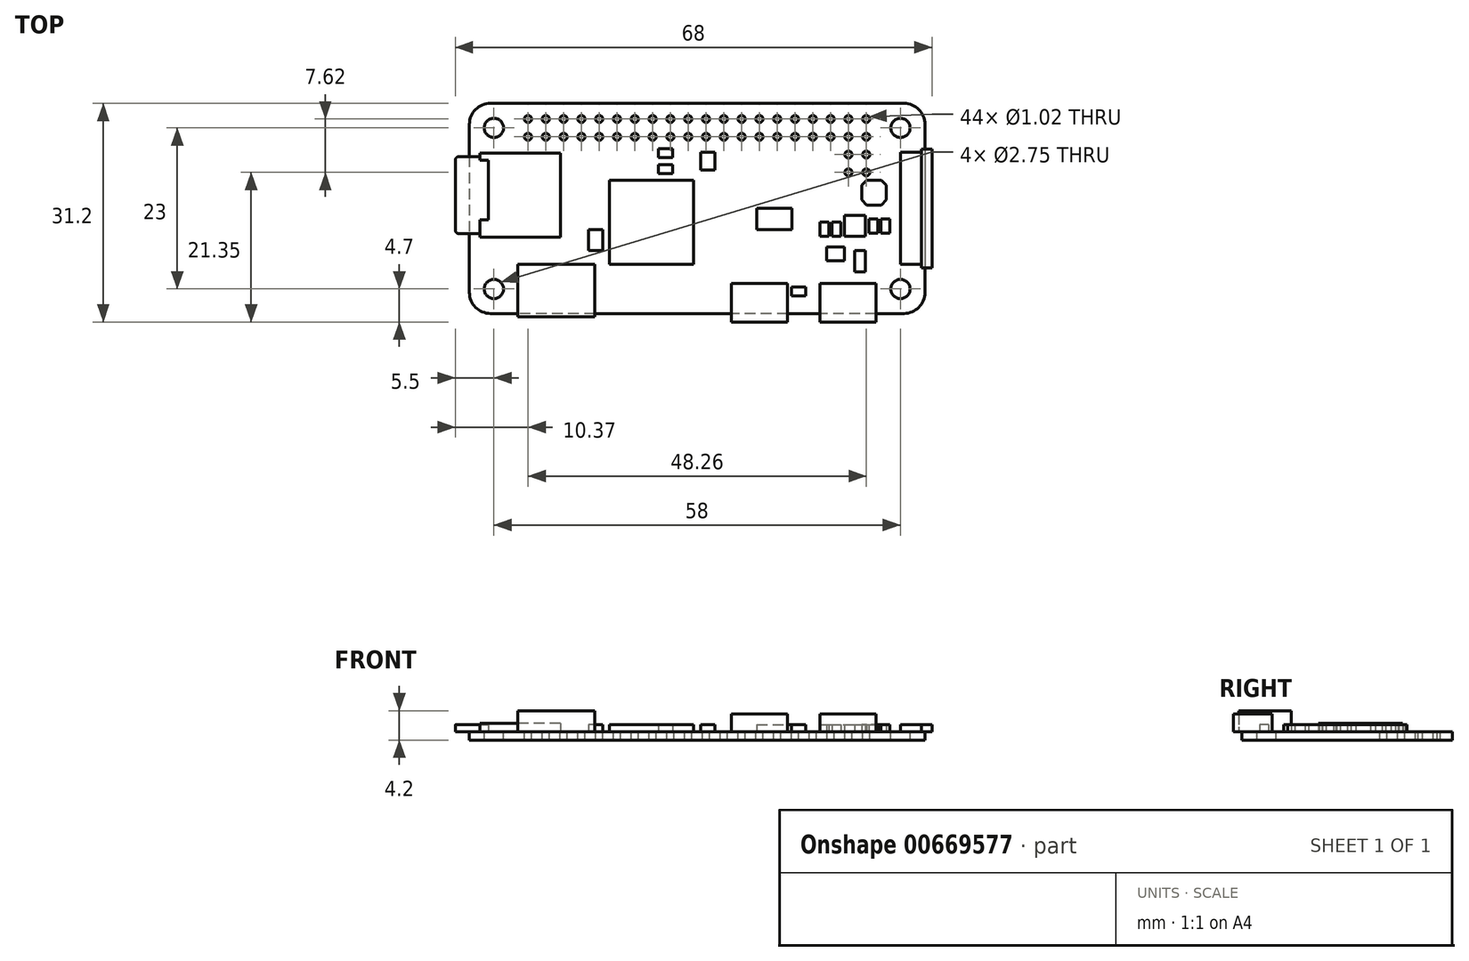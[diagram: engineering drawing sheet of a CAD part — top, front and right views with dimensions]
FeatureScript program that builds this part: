
annotation { "Feature Type Name" : "Feature", "Feature Type Description" : "" }
export const myFeature = defineFeature(function(context is Context, id is Id, definition is map)
    precondition{}
    {
        {
            var Q0;
            Q0=qCreatedBy(makeId("Top.planeOp"),FACE);
            var sketch = newSketch(context, id + "F0", { "sketchPlane" : qUnion([Q0])});
            skLineSegment(sketch, "E0.bottom", {"start": v(29.5, 15) * mm, "end": v(-29.5, 15) * mm});
            skLineSegment(sketch, "E0.top", {"start": v(29.5, -15) * mm, "end": v(-29.5, -15) * mm});
            skLineSegment(sketch, "E0.left", {"start": v(32.5, 12) * mm, "end": v(32.5, -12) * mm});
            skLineSegment(sketch, "E0.right", {"start": v(-32.5, 12) * mm, "end": v(-32.5, -12) * mm});
            skPoint(sketch, "E0.middle", {"position": v(0, 0) * mm});
            skPoint(sketch, "E1.visualSharp", {"position": v(-32.5, 15) * mm});
            skArc(sketch, "E1.filletArc", {"start": v(-29.5, 15) * mm, "mid": v(-31.62, 14.12) * mm, "end": v(-32.5, 12) * mm});
            skPoint(sketch, "E2.visualSharp", {"position": v(32.5, 15) * mm});
            skArc(sketch, "E2.filletArc", {"start": v(32.5, 12) * mm, "mid": v(31.62, 14.12) * mm, "end": v(29.5, 15) * mm});
            skPoint(sketch, "E3.visualSharp", {"position": v(32.5, -15) * mm});
            skArc(sketch, "E3.filletArc", {"start": v(29.5, -15) * mm, "mid": v(31.62, -14.12) * mm, "end": v(32.5, -12) * mm});
            skPoint(sketch, "E4.visualSharp", {"position": v(-32.5, -15) * mm});
            skArc(sketch, "E4.filletArc", {"start": v(-32.5, -12) * mm, "mid": v(-31.62, -14.12) * mm, "end": v(-29.5, -15) * mm});
            skLineSegment(sketch, "E5.bottom", {"start": v(29, 11.5) * mm, "end": v(-29, 11.5) * mm, "construction": true});
            skLineSegment(sketch, "E5.top", {"start": v(29, -11.5) * mm, "end": v(-29, -11.5) * mm, "construction": true});
            skLineSegment(sketch, "E5.left", {"start": v(29, 11.5) * mm, "end": v(29, -11.5) * mm, "construction": true});
            skLineSegment(sketch, "E5.right", {"start": v(-29, 11.5) * mm, "end": v(-29, -11.5) * mm, "construction": true});
            skCircle(sketch, "E6", {"center": v(29, 11.5) * mm, "radius": 3 * mm});
            skCircle(sketch, "E7", {"center": v(29, 11.5) * mm, "radius": 1.38 * mm});
            skCircle(sketch, "E8", {"center": v(-29, 11.5) * mm, "radius": 1.38 * mm});
            skCircle(sketch, "E9", {"center": v(-29, 11.5) * mm, "radius": 3 * mm});
            skCircle(sketch, "E10", {"center": v(-29, -11.5) * mm, "radius": 3 * mm});
            skCircle(sketch, "E11", {"center": v(-29, -11.5) * mm, "radius": 1.38 * mm});
            skCircle(sketch, "E12", {"center": v(29, -11.5) * mm, "radius": 1.38 * mm});
            skCircle(sketch, "E13", {"center": v(29, -11.5) * mm, "radius": 3 * mm});
            skCircle(sketch, "E14", {"center": v(24.13, 12.77) * mm, "radius": 0.5 * mm});
            skCircle(sketch, "E15", {"center": v(24.13, 10.23) * mm, "radius": 0.5 * mm});
            skLineSegment(sketch, "E16", {"start": v(24.13, 12.77) * mm, "end": v(24.13, 10.23) * mm, "construction": true});
            skPoint(sketch, "E17", {"position": v(24.13, 11.5) * mm});
            skCircle(sketch, "E18.1.0.0", {"center": v(21.59, 12.77) * mm, "radius": 0.5 * mm});
            skCircle(sketch, "E18.1.0.1", {"center": v(21.59, 10.23) * mm, "radius": 0.5 * mm});
            skCircle(sketch, "E18.2.0.0", {"center": v(19.05, 12.77) * mm, "radius": 0.5 * mm});
            skCircle(sketch, "E18.2.0.1", {"center": v(19.05, 10.23) * mm, "radius": 0.5 * mm});
            skCircle(sketch, "E18.3.0.0", {"center": v(16.5, 12.77) * mm, "radius": 0.5 * mm});
            skCircle(sketch, "E18.3.0.1", {"center": v(16.5, 10.23) * mm, "radius": 0.5 * mm});
            skCircle(sketch, "E18.4.0.0", {"center": v(13.97, 12.77) * mm, "radius": 0.5 * mm});
            skCircle(sketch, "E18.4.0.1", {"center": v(13.97, 10.23) * mm, "radius": 0.5 * mm});
            skCircle(sketch, "E18.5.0.0", {"center": v(11.43, 12.77) * mm, "radius": 0.5 * mm});
            skCircle(sketch, "E18.5.0.1", {"center": v(11.43, 10.23) * mm, "radius": 0.5 * mm});
            skCircle(sketch, "E18.6.0.0", {"center": v(8.89, 12.77) * mm, "radius": 0.5 * mm});
            skCircle(sketch, "E18.6.0.1", {"center": v(8.89, 10.23) * mm, "radius": 0.5 * mm});
            skCircle(sketch, "E18.7.0.0", {"center": v(6.35, 12.77) * mm, "radius": 0.5 * mm});
            skCircle(sketch, "E18.7.0.1", {"center": v(6.35, 10.23) * mm, "radius": 0.5 * mm});
            skCircle(sketch, "E18.8.0.0", {"center": v(3.8, 12.77) * mm, "radius": 0.5 * mm});
            skCircle(sketch, "E18.8.0.1", {"center": v(3.8, 10.23) * mm, "radius": 0.5 * mm});
            skCircle(sketch, "E18.9.0.0", {"center": v(1.27, 12.77) * mm, "radius": 0.5 * mm});
            skCircle(sketch, "E18.9.0.1", {"center": v(1.27, 10.23) * mm, "radius": 0.5 * mm});
            skCircle(sketch, "E18.10.0.0", {"center": v(-1.27, 12.77) * mm, "radius": 0.5 * mm});
            skCircle(sketch, "E18.10.0.1", {"center": v(-1.27, 10.23) * mm, "radius": 0.5 * mm});
            skCircle(sketch, "E18.11.0.0", {"center": v(-3.81, 12.77) * mm, "radius": 0.5 * mm});
            skCircle(sketch, "E18.11.0.1", {"center": v(-3.81, 10.23) * mm, "radius": 0.5 * mm});
            skCircle(sketch, "E18.12.0.0", {"center": v(-6.35, 12.77) * mm, "radius": 0.5 * mm});
            skCircle(sketch, "E18.12.0.1", {"center": v(-6.35, 10.23) * mm, "radius": 0.5 * mm});
            skCircle(sketch, "E18.13.0.0", {"center": v(-8.9, 12.77) * mm, "radius": 0.5 * mm});
            skCircle(sketch, "E18.13.0.1", {"center": v(-8.9, 10.23) * mm, "radius": 0.5 * mm});
            skCircle(sketch, "E18.14.0.0", {"center": v(-11.43, 12.77) * mm, "radius": 0.5 * mm});
            skCircle(sketch, "E18.14.0.1", {"center": v(-11.43, 10.23) * mm, "radius": 0.5 * mm});
            skCircle(sketch, "E18.15.0.0", {"center": v(-13.97, 12.77) * mm, "radius": 0.5 * mm});
            skCircle(sketch, "E18.15.0.1", {"center": v(-13.97, 10.23) * mm, "radius": 0.5 * mm});
            skCircle(sketch, "E18.16.0.0", {"center": v(-16.51, 12.77) * mm, "radius": 0.5 * mm});
            skCircle(sketch, "E18.16.0.1", {"center": v(-16.51, 10.23) * mm, "radius": 0.5 * mm});
            skCircle(sketch, "E18.17.0.0", {"center": v(-19.05, 12.77) * mm, "radius": 0.5 * mm});
            skCircle(sketch, "E18.17.0.1", {"center": v(-19.05, 10.23) * mm, "radius": 0.5 * mm});
            skCircle(sketch, "E18.18.0.0", {"center": v(-21.6, 12.77) * mm, "radius": 0.5 * mm});
            skCircle(sketch, "E18.18.0.1", {"center": v(-21.6, 10.23) * mm, "radius": 0.5 * mm});
            skCircle(sketch, "E18.19.0.0", {"center": v(-24.13, 12.77) * mm, "radius": 0.5 * mm});
            skCircle(sketch, "E18.19.0.1", {"center": v(-24.13, 10.23) * mm, "radius": 0.5 * mm});
            skLineSegment(sketch, "E18.direction1", {"start": v(24.13, 12.77) * mm, "end": v(21.59, 12.77) * mm, "construction": true});
            skCircle(sketch, "E19.1.0.0", {"center": v(21.59, 7.69) * mm, "radius": 0.5 * mm});
            skCircle(sketch, "E19.1.0.1", {"center": v(24.13, 7.69) * mm, "radius": 0.5 * mm});
            skCircle(sketch, "E19.1.0.2", {"center": v(24.13, 5.15) * mm, "radius": 0.5 * mm});
            skCircle(sketch, "E19.1.0.3", {"center": v(21.59, 5.15) * mm, "radius": 0.5 * mm});
            skLineSegment(sketch, "E19.direction1", {"start": v(21.59, 12.77) * mm, "end": v(21.59, 7.69) * mm, "construction": true});
            skSolve(sketch);
        }
        {
            var Q0;
            Q0=qCreatedBy(makeId("Top.planeOp"),FACE);
            var sketch = newSketch(context, id + "F1", { "sketchPlane" : qUnion([Q0])});
            skLineSegment(sketch, "E20.bottom", {"start": v(33.5, -8.5) * mm, "end": v(32, -8.5) * mm});
            skLineSegment(sketch, "E20.top", {"start": v(33.5, 8.5) * mm, "end": v(32, 8.5) * mm});
            skLineSegment(sketch, "E20.left", {"start": v(33.5, -8.5) * mm, "end": v(33.5, 8.5) * mm});
            skLineSegment(sketch, "E20.right", {"start": v(32, -8.5) * mm, "end": v(32, 8.5) * mm});
            skPoint(sketch, "E20.middle", {"position": v(32.75, 0) * mm});
            skLineSegment(sketch, "E21.bottom", {"start": v(-14.6, -15.5) * mm, "end": v(-25.6, -15.5) * mm});
            skLineSegment(sketch, "E21.top", {"start": v(-14.6, -8) * mm, "end": v(-25.6, -8) * mm});
            skLineSegment(sketch, "E21.left", {"start": v(-14.6, -15.5) * mm, "end": v(-14.6, -8) * mm});
            skLineSegment(sketch, "E21.right", {"start": v(-25.6, -15.5) * mm, "end": v(-25.6, -8) * mm});
            skPoint(sketch, "E21.middle", {"position": v(-20.1, -11.75) * mm});
            skLineSegment(sketch, "E22.bottom", {"start": v(12.9, -16.2) * mm, "end": v(4.9, -16.2) * mm});
            skLineSegment(sketch, "E22.top", {"start": v(12.9, -10.7) * mm, "end": v(4.9, -10.7) * mm});
            skLineSegment(sketch, "E22.left", {"start": v(12.9, -16.2) * mm, "end": v(12.9, -10.7) * mm});
            skLineSegment(sketch, "E22.right", {"start": v(4.9, -16.2) * mm, "end": v(4.9, -10.7) * mm});
            skPoint(sketch, "E22.middle", {"position": v(8.9, -13.45) * mm});
            skLineSegment(sketch, "E23.bottom", {"start": v(25.5, -16.2) * mm, "end": v(17.5, -16.2) * mm});
            skLineSegment(sketch, "E23.top", {"start": v(25.5, -10.7) * mm, "end": v(17.5, -10.7) * mm});
            skLineSegment(sketch, "E23.left", {"start": v(25.5, -16.2) * mm, "end": v(25.5, -10.7) * mm});
            skLineSegment(sketch, "E23.right", {"start": v(17.5, -16.2) * mm, "end": v(17.5, -10.7) * mm});
            skPoint(sketch, "E23.middle", {"position": v(21.5, -13.45) * mm});
            skLineSegment(sketch, "E24.bottom", {"start": v(-19.5, 7.9) * mm, "end": v(-31, 7.9) * mm});
            skLineSegment(sketch, "E24.top", {"start": v(-19.5, -4.1) * mm, "end": v(-31, -4.1) * mm});
            skLineSegment(sketch, "E24.left", {"start": v(-19.5, 7.9) * mm, "end": v(-19.5, -4.1) * mm});
            skLineSegment(sketch, "E24.right", {"start": v(-31, 7.9) * mm, "end": v(-31, -4.1) * mm});
            skPoint(sketch, "E24.middle", {"position": v(-25.25, 1.9) * mm});
            skLineSegment(sketch, "E25", {"start": v(-31, 7.4) * mm, "end": v(-34, 7.4) * mm});
            skLineSegment(sketch, "E26", {"start": v(-34.5, 6.9) * mm, "end": v(-34.5, -3.1) * mm});
            skLineSegment(sketch, "E27", {"start": v(-34, -3.6) * mm, "end": v(-31, -3.6) * mm});
            skPoint(sketch, "E28.visualSharp", {"position": v(-34.5, 7.4) * mm});
            skArc(sketch, "E28.filletArc", {"start": v(-34, 7.4) * mm, "mid": v(-34.35, 7.25) * mm, "end": v(-34.5, 6.9) * mm});
            skPoint(sketch, "E29.visualSharp", {"position": v(-34.5, -3.6) * mm});
            skArc(sketch, "E29.filletArc", {"start": v(-34.5, -3.1) * mm, "mid": v(-34.35, -3.45) * mm, "end": v(-34, -3.6) * mm});
            skPoint(sketch, "E30", {"position": v(-34.5, 1.9) * mm});
            skLineSegment(sketch, "E31", {"start": v(-31, 6.9) * mm, "end": v(-29.8, 6.9) * mm});
            skLineSegment(sketch, "E32", {"start": v(-29.8, 6.9) * mm, "end": v(-29.8, -1.6) * mm});
            skLineSegment(sketch, "E33", {"start": v(-29.8, -1.6) * mm, "end": v(-31, -1.6) * mm});
            skLineSegment(sketch, "E34", {"start": v(32, 8) * mm, "end": v(29, 8) * mm});
            skLineSegment(sketch, "E35", {"start": v(29, 8) * mm, "end": v(29, -8) * mm});
            skLineSegment(sketch, "E36", {"start": v(29, -8) * mm, "end": v(32, -8) * mm});
            skLineSegment(sketch, "E37", {"start": v(32.75, 0) * mm, "end": v(29, 0) * mm, "construction": true});
            skSolve(sketch);
        }
        {
            var Q0;
            Q0=qCreatedBy(makeId("Top.planeOp"),FACE);
            var sketch = newSketch(context, id + "F2", { "sketchPlane" : qUnion([Q0])});
            skLineSegment(sketch, "E38.bottom", {"start": v(-12.5, -8) * mm, "end": v(-0.5, -8) * mm});
            skLineSegment(sketch, "E38.top", {"start": v(-12.5, 4) * mm, "end": v(-0.5, 4) * mm});
            skLineSegment(sketch, "E38.left", {"start": v(-12.5, -8) * mm, "end": v(-12.5, 4) * mm});
            skLineSegment(sketch, "E38.right", {"start": v(-0.5, -8) * mm, "end": v(-0.5, 4) * mm});
            skLineSegment(sketch, "E39.bottom", {"start": v(-5.53, 8.54) * mm, "end": v(-3.5, 8.54) * mm});
            skLineSegment(sketch, "E39.top", {"start": v(-5.53, 7.27) * mm, "end": v(-3.5, 7.27) * mm});
            skLineSegment(sketch, "E39.left", {"start": v(-5.53, 8.54) * mm, "end": v(-5.53, 7.27) * mm});
            skLineSegment(sketch, "E39.right", {"start": v(-3.5, 8.54) * mm, "end": v(-3.5, 7.27) * mm});
            skLineSegment(sketch, "E40.bottom", {"start": v(-5.53, 6.27) * mm, "end": v(-3.5, 6.27) * mm});
            skLineSegment(sketch, "E40.top", {"start": v(-5.53, 5) * mm, "end": v(-3.5, 5) * mm});
            skLineSegment(sketch, "E40.left", {"start": v(-5.53, 6.27) * mm, "end": v(-5.53, 5) * mm});
            skLineSegment(sketch, "E40.right", {"start": v(-3.5, 6.27) * mm, "end": v(-3.5, 5) * mm});
            skLineSegment(sketch, "E41.bottom", {"start": v(13.47, -11.23) * mm, "end": v(15.5, -11.23) * mm});
            skLineSegment(sketch, "E41.top", {"start": v(13.47, -12.5) * mm, "end": v(15.5, -12.5) * mm});
            skLineSegment(sketch, "E41.left", {"start": v(13.47, -11.23) * mm, "end": v(13.47, -12.5) * mm});
            skLineSegment(sketch, "E41.right", {"start": v(15.5, -11.23) * mm, "end": v(15.5, -12.5) * mm});
            skLineSegment(sketch, "E42.bottom", {"start": v(17.5, -1.97) * mm, "end": v(18.77, -1.97) * mm});
            skLineSegment(sketch, "E42.top", {"start": v(17.5, -4) * mm, "end": v(18.77, -4) * mm});
            skLineSegment(sketch, "E42.left", {"start": v(17.5, -1.97) * mm, "end": v(17.5, -4) * mm});
            skLineSegment(sketch, "E42.right", {"start": v(18.77, -1.97) * mm, "end": v(18.77, -4) * mm});
            skLineSegment(sketch, "E43.bottom", {"start": v(19.25, -1.97) * mm, "end": v(20.52, -1.97) * mm});
            skLineSegment(sketch, "E43.top", {"start": v(19.25, -4) * mm, "end": v(20.52, -4) * mm});
            skLineSegment(sketch, "E43.left", {"start": v(19.25, -1.97) * mm, "end": v(19.25, -4) * mm});
            skLineSegment(sketch, "E43.right", {"start": v(20.52, -1.97) * mm, "end": v(20.52, -4) * mm});
            skLineSegment(sketch, "E44.bottom", {"start": v(24.48, -1.48) * mm, "end": v(25.75, -1.48) * mm});
            skLineSegment(sketch, "E44.top", {"start": v(24.48, -3.52) * mm, "end": v(25.75, -3.52) * mm});
            skLineSegment(sketch, "E44.left", {"start": v(24.48, -1.48) * mm, "end": v(24.48, -3.52) * mm});
            skLineSegment(sketch, "E44.right", {"start": v(25.75, -1.48) * mm, "end": v(25.75, -3.52) * mm});
            skLineSegment(sketch, "E45.bottom", {"start": v(26.23, -1.48) * mm, "end": v(27.5, -1.48) * mm});
            skLineSegment(sketch, "E45.top", {"start": v(26.23, -3.52) * mm, "end": v(27.5, -3.52) * mm});
            skLineSegment(sketch, "E45.left", {"start": v(26.23, -1.48) * mm, "end": v(26.23, -3.52) * mm});
            skLineSegment(sketch, "E45.right", {"start": v(27.5, -1.48) * mm, "end": v(27.5, -3.52) * mm});
            skLineSegment(sketch, "E46.bottom", {"start": v(-13.5, -3) * mm, "end": v(-15.5, -3) * mm});
            skLineSegment(sketch, "E46.top", {"start": v(-13.5, -6) * mm, "end": v(-15.5, -6) * mm});
            skLineSegment(sketch, "E46.left", {"start": v(-13.5, -3) * mm, "end": v(-13.5, -6) * mm});
            skLineSegment(sketch, "E46.right", {"start": v(-15.5, -3) * mm, "end": v(-15.5, -6) * mm});
            skLineSegment(sketch, "E47.bottom", {"start": v(8.5, 0) * mm, "end": v(13.5, 0) * mm});
            skLineSegment(sketch, "E47.top", {"start": v(8.5, -3) * mm, "end": v(13.5, -3) * mm});
            skLineSegment(sketch, "E47.left", {"start": v(8.5, 0) * mm, "end": v(8.5, -3) * mm});
            skLineSegment(sketch, "E47.right", {"start": v(13.5, 0) * mm, "end": v(13.5, -3) * mm});
            skLineSegment(sketch, "E48.bottom", {"start": v(21, -1) * mm, "end": v(24, -1) * mm});
            skLineSegment(sketch, "E48.top", {"start": v(21, -4) * mm, "end": v(24, -4) * mm});
            skLineSegment(sketch, "E48.left", {"start": v(21, -1) * mm, "end": v(21, -4) * mm});
            skLineSegment(sketch, "E48.right", {"start": v(24, -1) * mm, "end": v(24, -4) * mm});
            skLineSegment(sketch, "E49.bottom", {"start": v(0.5, 8) * mm, "end": v(2.5, 8) * mm});
            skLineSegment(sketch, "E49.top", {"start": v(0.5, 5.5) * mm, "end": v(2.5, 5.5) * mm});
            skLineSegment(sketch, "E49.left", {"start": v(0.5, 8) * mm, "end": v(0.5, 5.5) * mm});
            skLineSegment(sketch, "E49.right", {"start": v(2.5, 8) * mm, "end": v(2.5, 5.5) * mm});
            skLineSegment(sketch, "E50.bottom", {"start": v(18.5, -5.5) * mm, "end": v(21, -5.5) * mm});
            skLineSegment(sketch, "E50.top", {"start": v(18.5, -7.5) * mm, "end": v(21, -7.5) * mm});
            skLineSegment(sketch, "E50.left", {"start": v(18.5, -5.5) * mm, "end": v(18.5, -7.5) * mm});
            skLineSegment(sketch, "E50.right", {"start": v(21, -5.5) * mm, "end": v(21, -7.5) * mm});
            skLineSegment(sketch, "E51.bottom", {"start": v(22.48, -6) * mm, "end": v(24, -6) * mm});
            skLineSegment(sketch, "E51.top", {"start": v(22.48, -9.05) * mm, "end": v(24, -9.05) * mm});
            skLineSegment(sketch, "E51.left", {"start": v(22.48, -6) * mm, "end": v(22.48, -9.05) * mm});
            skLineSegment(sketch, "E51.right", {"start": v(24, -6) * mm, "end": v(24, -9.05) * mm});
            skLineSegment(sketch, "E52", {"start": v(24, -2.5) * mm, "end": v(24.48, -2.5) * mm, "construction": true});
            skLineSegment(sketch, "E53", {"start": v(26.23, -3.52) * mm, "end": v(25.75, -3.52) * mm, "construction": true});
            skLineSegment(sketch, "E54", {"start": v(21, -4) * mm, "end": v(20.52, -4) * mm, "construction": true});
            skLineSegment(sketch, "E55", {"start": v(19.25, -4) * mm, "end": v(18.77, -4) * mm, "construction": true});
            skLineSegment(sketch, "E56", {"start": v(23.5, 3.3) * mm, "end": v(23.5, 1.2) * mm});
            skLineSegment(sketch, "E57", {"start": v(23.5, 1.2) * mm, "end": v(24.2, 0.5) * mm});
            skLineSegment(sketch, "E58", {"start": v(24.2, 0.5) * mm, "end": v(26.3, 0.5) * mm});
            skLineSegment(sketch, "E59", {"start": v(26.3, 0.5) * mm, "end": v(27, 1.2) * mm});
            skLineSegment(sketch, "E60", {"start": v(27, 1.2) * mm, "end": v(27, 3.3) * mm});
            skLineSegment(sketch, "E61", {"start": v(27, 3.3) * mm, "end": v(26.3, 4) * mm});
            skLineSegment(sketch, "E62", {"start": v(26.3, 4) * mm, "end": v(24.2, 4) * mm});
            skLineSegment(sketch, "E63", {"start": v(24.2, 4) * mm, "end": v(23.5, 3.3) * mm});
            skSolve(sketch);
        }
        {
            var Q0;
            Q0=qSketchRegion(id+"F0",true);
            var Q1;
            Q1=makeQuery(id+"F0.imprint","IMPRINT",FACE,{"disambiguationData":[TD([[makeQuery(id+"F0.imprint","IMPRINT",EDGE,{"derivedFrom":sQuery(id+"F0.wireOp",EDGE,"E10")}),1.0]])]});
            var Q2;
            Q2=makeQuery(id+"F0.imprint","IMPRINT",FACE,{"disambiguationData":[TD([[makeQuery(id+"F0.imprint","IMPRINT",EDGE,{"derivedFrom":sQuery(id+"F0.wireOp",EDGE,"E8")}),-1.0]])]});
            var Q3;
            Q3=makeQuery(id+"F0.imprint","IMPRINT",FACE,{"disambiguationData":[TD([[makeQuery(id+"F0.imprint","IMPRINT",EDGE,{"derivedFrom":sQuery(id+"F0.wireOp",EDGE,"E6")}),1.0]])]});
            var Q4;
            Q4=makeQuery(id+"F0.imprint","IMPRINT",FACE,{"disambiguationData":[TD([[makeQuery(id+"F0.imprint","IMPRINT",EDGE,{"derivedFrom":sQuery(id+"F0.wireOp",EDGE,"E12")}),-1.0]])]});
            extrude(context, id + "F3", {"entities" : qUnion([Q0, Q1, Q2, Q3, Q4]), "oppositeDirection" : true, "depth" : 1.2 * mm, "offsetDistance" : 25 * mm});
        }
        {
            var Q0;
            Q0=makeQuery(id+"F1.imprint","IMPRINT",FACE,{"disambiguationData":[TD([[makeQuery(id+"F1.imprint","IMPRINT",EDGE,{"derivedFrom":sQuery(id+"F1.wireOp",EDGE,"E20.bottom")}),-1.0]])]});
            extrude(context, id + "F4", {"entities" : qUnion([Q0]), "depth" : 1 * mm, "offsetDistance" : 25 * mm});
        }
        {
            var Q0;
            {var subQ0=sQuery(id+"F1.wireOp",EDGE,"E34");Q0=makeQuery(id+"F1.imprint","IMPRINT",FACE,{"disambiguationData":[TD([[makeQuery(id+"F1.imprint","IMPRINT",EDGE,{"derivedFrom":subQ0}),1.0]])]});}
            extrude(context, id + "F5", {"entities" : qUnion([Q0]), "depth" : 1 * mm, "offsetDistance" : 25 * mm});
        }
        {
            var Q0;
            Q0=makeQuery(id+"F1.imprint","IMPRINT",FACE,{"disambiguationData":[TD([[makeQuery(id+"F1.imprint","IMPRINT",EDGE,{"derivedFrom":sQuery(id+"F1.wireOp",EDGE,"E23.bottom")}),-1.0]])]});
            var Q1;
            Q1=makeQuery(id+"F1.imprint","IMPRINT",FACE,{"disambiguationData":[TD([[makeQuery(id+"F1.imprint","IMPRINT",EDGE,{"derivedFrom":sQuery(id+"F1.wireOp",EDGE,"E22.bottom")}),-1.0]])]});
            extrude(context, id + "F6", {"entities" : qUnion([Q0, Q1]), "depth" : 2.5 * mm, "offsetDistance" : 25 * mm});
        }
        {
            var Q0;
            Q0=makeQuery(id+"F1.imprint","IMPRINT",FACE,{"disambiguationData":[TD([[makeQuery(id+"F1.imprint","IMPRINT",EDGE,{"derivedFrom":sQuery(id+"F1.wireOp",EDGE,"E21.bottom")}),-1.0]])]});
            extrude(context, id + "F7", {"entities" : qUnion([Q0]), "depth" : 3 * mm, "offsetDistance" : 25 * mm});
        }
        {
            var Q0;
            {var subQ1=sQuery(id+"F1.wireOp",EDGE,"E24.bottom");Q0=makeQuery(id+"F1.imprint","IMPRINT",FACE,{"disambiguationData":[TD([[makeQuery(id+"F1.imprint","IMPRINT",EDGE,{"derivedFrom":subQ1}),1.0]])]});}
            extrude(context, id + "F8", {"entities" : qUnion([Q0]), "depth" : 1.2 * mm, "offsetDistance" : 25 * mm});
        }
        {
            var Q0;
            {var subQ0=sQuery(id+"F1.wireOp",EDGE,"E31");Q0=makeQuery(id+"F1.imprint","IMPRINT",FACE,{"disambiguationData":[TD([[makeQuery(id+"F1.imprint","IMPRINT",EDGE,{"derivedFrom":subQ0}),-1.0]])]});}
            var Q1;
            {var subQ0=sQuery(id+"F1.wireOp",EDGE,"E25");Q1=makeQuery(id+"F1.imprint","IMPRINT",FACE,{"disambiguationData":[TD([[makeQuery(id+"F1.imprint","IMPRINT",EDGE,{"derivedFrom":subQ0}),1.0]])]});}
            extrude(context, id + "F9", {"entities" : qUnion([Q0, Q1]), "depth" : 1 * mm, "offsetDistance" : 25 * mm});
        }
        {
            var Q0;
            Q0=qSketchRegion(id+"F2",true);
            extrude(context, id + "F10", {"entities" : qUnion([Q0]), "depth" : 1 * mm, "offsetDistance" : 25 * mm});
        }
    });
